# Revit family: Window-Single_&_Double_Hung-Kawneer-8450TL
name_source: partatom
category: Windows
revit_build: Autodesk Revit 2015 (Build: 20140905_0730(x64)
units: mm (PartAtom-declared; Revit-internal decimal feet)

## types (1)
- Double Hung
    Assembly Code = B2020100
    Bottom Fixed Window = No
    Description = Kawneer 8450TL Double Hung Window
    Double Window = No
    Fixed Panel Second Window = No
    Frame Finish = Paint - Kawneer - White
    Frame Material = Wood - Kawneer - Oak
    Frame Type = Frame-Double_Hung-Kawneer-8450TL : Frame
    Frame Type Second Window = Frame-Fixed-Kawneer-w_Muntins : Frame
    Frame Type Small Fixed = Frame-Fixed-Kawneer-wo_Muntins : Frame
    Glazing Material = Glass - Kawneer - Clear
    Hung Panel Second Window = Yes
    Keynote = 08500
    Manufacturer = Kawneer Company, Inc
    Model = 8450TL Double Hung
    Panel Type = Panel-Double_Hung-Kawneer-wo_Muntins-8450TL : w/o Muntins
    Panel Type Second Window = Panel-Fixed-Kawneer-w_Muntins-8410TL : w Muntins
    Panel Type Small Fixed = Panel-Fixed-Kawneer-wo_Muntins-8410TL : wo Muntins
    Product Documentation Link = http://www.kawneer.com
    Product Page URL = http://www.kawneer.com
    Product data url = https://bimobject.com
    Top Fixed Window = No
    URL = http://www.kawneer.com
    Wall Closure = By host

## geometry (parser evidence)
native form markers: Sweep x74
no freeform markers — native parametric forms only
